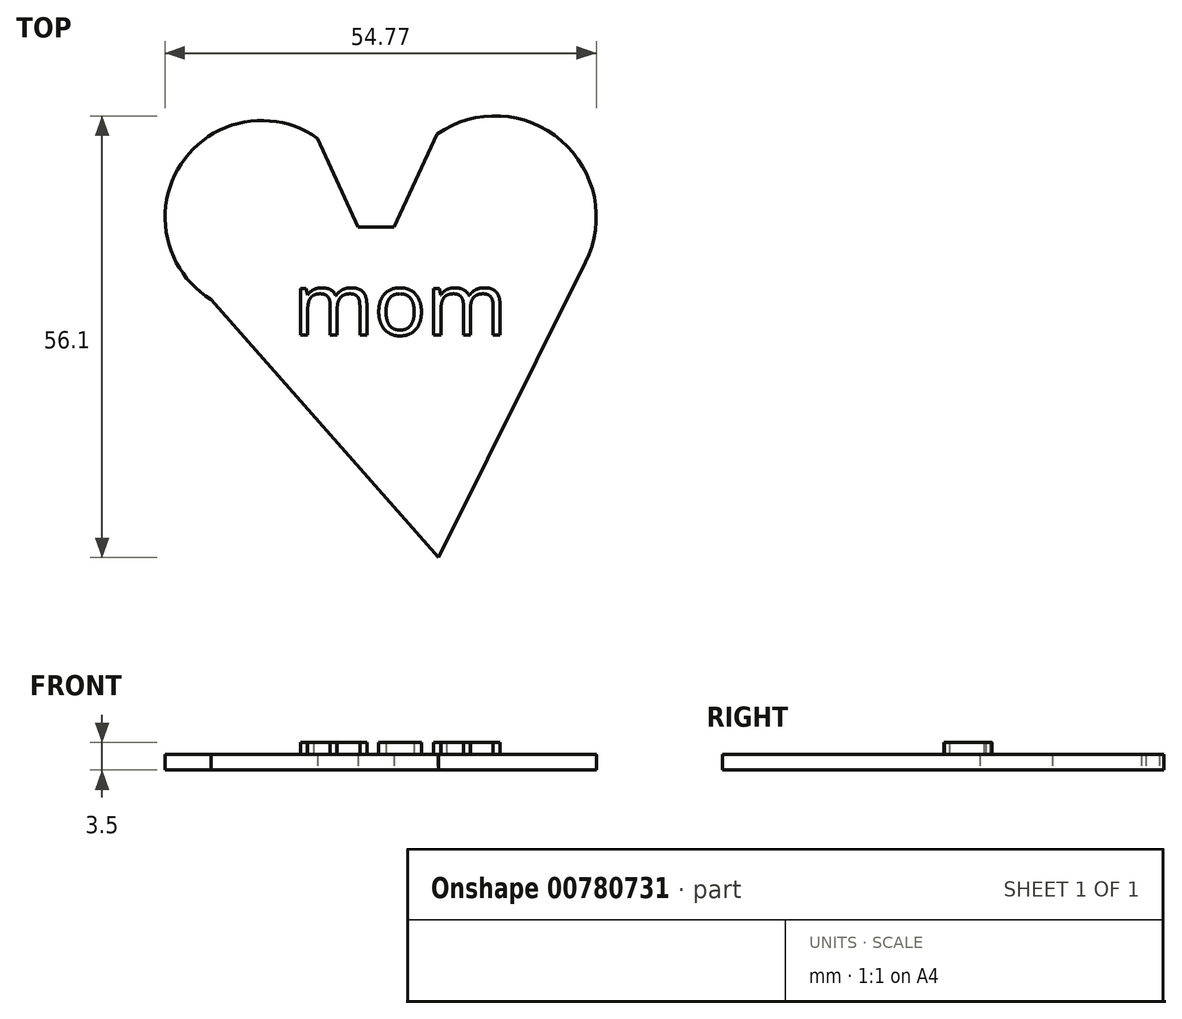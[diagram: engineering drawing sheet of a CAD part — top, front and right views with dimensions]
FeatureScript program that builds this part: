
annotation { "Feature Type Name" : "Feature", "Feature Type Description" : "" }
export const myFeature = defineFeature(function(context is Context, id is Id, definition is map)
    precondition{}
    {
        {
            var Q0;
            Q0=qCreatedBy(makeId("Top.planeOp"),FACE);
            var sketch = newSketch(context, id + "F0", { "sketchPlane" : qUnion([Q0])});
            skArc(sketch, "E0", {"start": v(-27.57, 53.25) * mm, "mid": v(-44.92, 50) * mm, "end": v(-41.12, 32.75) * mm});
            skArc(sketch, "E1", {"start": v(6.46, 37.51) * mm, "mid": v(3.35, 52.98) * mm, "end": v(-12.4, 53.8) * mm});
            skLineSegment(sketch, "E2", {"start": v(-27.57, 53.25) * mm, "end": v(-22.45, 41.95) * mm});
            skLineSegment(sketch, "E3", {"start": v(-22.45, 41.95) * mm, "end": v(-17.84, 41.95) * mm});
            skLineSegment(sketch, "E4", {"start": v(-17.84, 41.95) * mm, "end": v(-12.4, 53.8) * mm});
            skLineSegment(sketch, "E5", {"start": v(6.46, 37.51) * mm, "end": v(-12.22, 0) * mm});
            skLineSegment(sketch, "E6", {"start": v(-12.22, 0) * mm, "end": v(-41.12, 32.75) * mm});
            skSolve(sketch);
        }
        {
            var Q0;
            Q0=makeQuery(id+"F0.imprint","IMPRINT",FACE,{"disambiguationData":[TD([[makeQuery(id+"F0.imprint","IMPRINT",EDGE,{"derivedFrom":sQuery(id+"F0.wireOp",EDGE,"E0")}),1.0]])]});
            extrude(context, id + "F1", {"entities" : qUnion([Q0]), "depth" : 2 * mm, "offsetDistance" : 25.4 * mm});
        }
        {
            var Q0;
            Q0=makeQuery(id+"F1.opExtrude","CAP_FACE",FACE,{"disambiguationData":[OSD([sQuery(id+"F0.wireOp",EDGE,"E0"),sQuery(id+"F0.wireOp",EDGE,"E1"),sQuery(id+"F0.wireOp",EDGE,"E2"),sQuery(id+"F0.wireOp",EDGE,"E3"),sQuery(id+"F0.wireOp",EDGE,"E4"),sQuery(id+"F0.wireOp",EDGE,"E5"),sQuery(id+"F0.wireOp",EDGE,"E6")])],"isStart":false});
            var sketch = newSketch(context, id + "F2", { "sketchPlane" : qUnion([Q0])});
            skText(sketch, "E7", { "text": "mom\n", "fontName": "OpenSans-Regular.ttf"});
            const initialGuessF2  = {"E7": [-0.0307, 0.02825, 1, 0, 0.00794]};
            skSetInitialGuess(sketch, initialGuessF2);
            skSolve(sketch);
        }
        {
            var Q0;
            Q0 = qSketchRegion(id + "F2", true);
            extrude(context, id + "F3", {"entities" : qUnion([Q0]), "operationType" : NewBodyOperationType.ADD, "depth" : 1.5 * mm, "offsetDistance" : 25.4 * mm});
        }
    });
